# Revit family: РГП-50-ВВ
name_source: partatom
category: Арматура трубопроводов
units: mm (PartAtom-declared; Revit-internal decimal feet)

## family parameters
Всегда вертикально = Да
На основе рабочей плоскости = Нет
Общий = Нет
При загрузке вырезать с полостями = Нет
Размер круглого соединителя = Использовать диаметр
Тип детали = Клапан - Вставляется

## types (4) — shared parameters
ADSK_Единица измерения = шт.
ADSK_Завод-изготовитель = РУП "БЕЛГАЗТЕХНИКА"
ADSK_Количество = 1
ADSK_Марка = РГП-50
ADSK_Масса_Текст = 60,0 кг
ADSK_Тип соединения = фланцевый
zero-valued in all types: Отметка по умолчанию

## per-type parameters (varying)
| type | ADSK_Диапазон выходного давления, МПа | ADSK_Наименование |
| ВВ-(0,05-0,1) | 0,05-0,01 | Регулятор РГП-50-ВВ-(0,05-0,1) ТУ BY 100270876.161-2012 |
| ВВ-(0,1-0,3) | 0,1-0,3 | Регулятор РГП-50-ВВ-(0,1-0,3)  ТУ BY 100270876.161-2012 |
| ВВ-(0,01-0,05) | 0,01-0,05 | Регулятор РГП-50-ВВ-(0,01-0,05)  ТУ BY 100270876.161-2012 |
| ВВ-(0,3-0,6) | 0,3-0,6 | Регулятор РГП-50-ВВ-(0,3-0,6)  ТУ BY 100270876.161-2012 |
